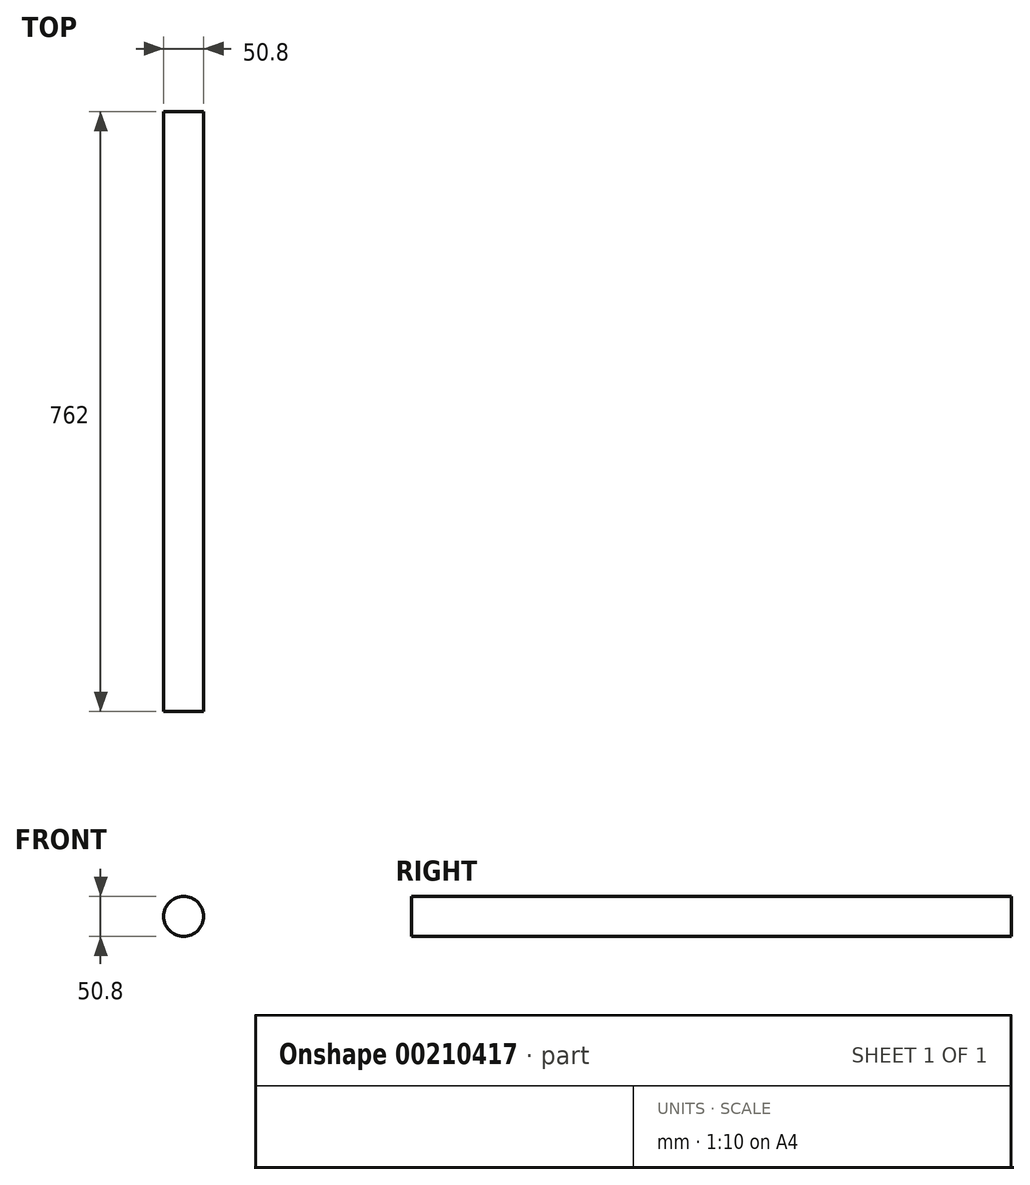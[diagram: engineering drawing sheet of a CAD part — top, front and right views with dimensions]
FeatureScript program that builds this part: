
annotation { "Feature Type Name" : "Feature", "Feature Type Description" : "" }
export const myFeature = defineFeature(function(context is Context, id is Id, definition is map)
    precondition{}
    {
        {
            var Q0;
            Q0=qCreatedBy(makeId("Front.planeOp"),FACE);
            var sketch = newSketch(context, id + "F0", { "sketchPlane" : qUnion([Q0])});
            skCircle(sketch, "E0", {"center": v(0, 0) * mm, "radius": 25.4 * mm});
            skSolve(sketch);
        }
        {
            var Q0;
            Q0=makeQuery(id+"F0.imprint","IMPRINT",FACE,{"disambiguationData":[TD([[makeQuery(id+"F0.imprint","IMPRINT",EDGE,{"derivedFrom":sQuery(id+"F0.wireOp",EDGE,"E0")}),1.0]])]});
            extrude(context, id + "F1", {"entities" : qUnion([Q0]), "depth" : 762 * mm});
        }
    });
